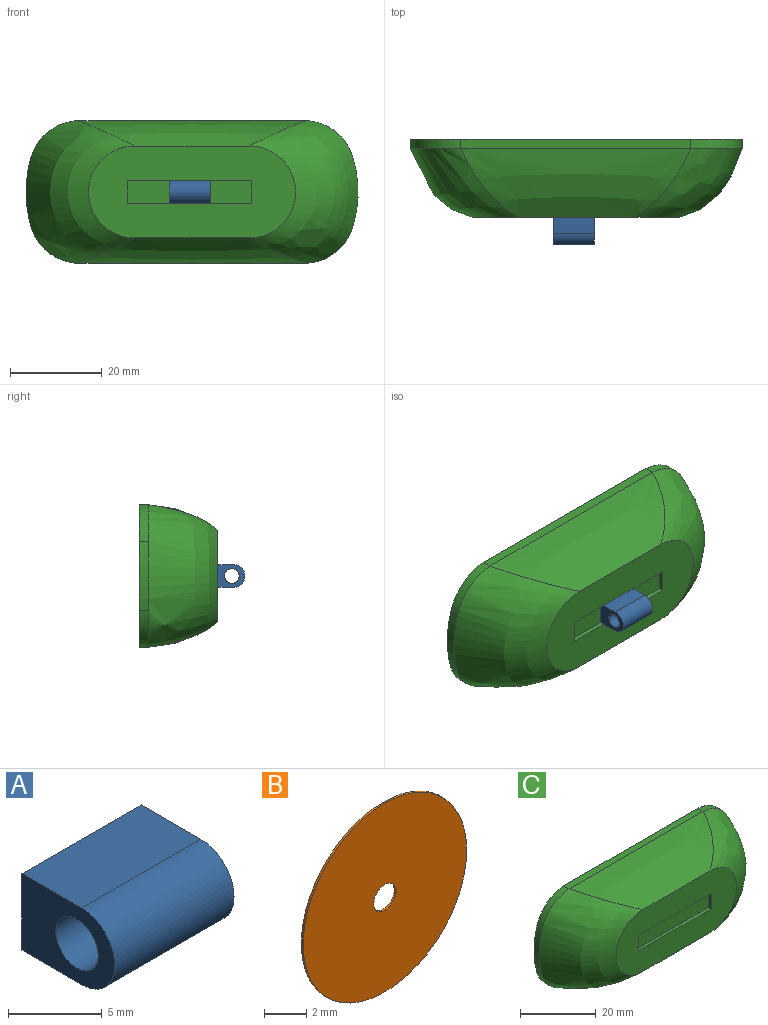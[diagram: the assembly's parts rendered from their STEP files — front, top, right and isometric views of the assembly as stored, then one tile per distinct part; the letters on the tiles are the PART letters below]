
ASSEMBLY  parts=3 mates=2
PART A: 7 faces, bbox 9x7x5 mm
  f0: plane 7x5mm, normal (1,0,0), area 24.3mm2, adj f1,f3,f4,f5,f6
  f1: plane 9x4.5mm, normal (0,0,1), area 40.5mm2, adj f0,f2,f4,f5
  f2: plane 7x5mm, normal (-1,0,0), area 24.3mm2, adj f1,f3,f4,f5,f6
  f3: plane 9x4.5mm, normal (0,0,-1), area 40.5mm2, adj f0,f2,f4,f5
  f4: plane 9x5mm, normal (0,1,0), area 45mm2, adj f0,f1,f2,f3
  f5: cylinder r=2.5mm len=9mm, axis (-1,0,0), area 70.7mm2, adj f0,f1,f2,f3
  f6: cylinder r=1.6mm len=9mm, axis (-1,0,0), area 90.5mm2, adj f0,f2
PART B: 4 faces, bbox 11x0.1x11 mm
  f0: cylinder r=0.75mm len=1.5mm, axis (0,-1,0), area 0.6mm2, adj f2,f3
  f1: cylinder r=5.5mm len=11mm, axis (0,-1,0), area 4.3mm2, adj f2,f3
  f2: plane 11x11mm, normal (0,1,0), area 93.3mm2, adj f0,f1
  f3: plane 11x11mm, normal (0,-1,0), area 93.3mm2, adj f0,f1
PART C: 58 faces, bbox 73.2x17.5x31.6 mm
  f0: plane 45.43x20.43mm, normal (0,-1,0), area 679.2mm2, adj f27,f28,f29,f30,f49,f50,f51,f57
  f1: cylinder r=5.5mm len=11mm, axis (0,-1,0), area 17.3mm2, adj f46,f47
  f2: cylinder r=5.75mm len=11.5mm, axis (0,-1,0), area 18.1mm2, adj f45,f46
  f3: cylinder r=6mm len=12mm, axis (0,1,0), area 37.7mm2, adj f35,f45
  f4: cylinder r=0.5mm len=2mm, axis (0,1,0), area 6.3mm2, adj f35,f36
  f5: cylinder r=0.5mm len=2mm, axis (0,1,0), area 6.3mm2, adj f35,f37
  f6: cylinder r=0.5mm len=2mm, axis (0,1,0), area 6.3mm2, adj f35,f38
  f7: cylinder r=0.5mm len=2mm, axis (0,1,0), area 6.3mm2, adj f35,f39
  f8: cylinder r=0.5mm len=2mm, axis (0,1,0), area 6.3mm2, adj f35,f40
  f9: cylinder r=0.5mm len=2mm, axis (0,1,0), area 6.3mm2, adj f35,f41
  f10: cylinder r=0.5mm len=2mm, axis (0,1,0), area 6.3mm2, adj f35,f42
  f11: cylinder r=0.5mm len=2mm, axis (0,1,0), area 6.3mm2, adj f35,f43
  f12: cylinder r=0.5mm len=2mm, axis (0,1,0), area 6.3mm2, adj f35,f44
  f13: extruded ~15x2mm, area 30.4mm2, adj f14,f20,f21,f30
  f14: cylinder r=11.22mm len=10mm, axis (0,-1,0), area 27.3mm2, adj f13,f15,f21,f30
  f15: plane 50.54x2.54mm, normal (0,0,1), area 100mm2, adj f14,f16,f21,f27
  f16: cylinder r=11.22mm len=10mm, axis (0,-1,0), area 27.3mm2, adj f15,f17,f21,f28
  f17: extruded ~15x2mm, area 30.5mm2, adj f16,f18,f21,f28
  f18: cylinder r=11.22mm len=10mm, axis (0,-1,0), area 27.3mm2, adj f17,f19,f21,f28
  f19: plane 50.54x2.54mm, normal (0,0,-1), area 100mm2, adj f18,f20,f21,f29
  f20: cylinder r=11.22mm len=10mm, axis (0,-1,0), area 27.3mm2, adj f13,f19,f21,f30
  f21: plane 72.64x31mm, normal (0,1,0), area 1626.5mm2, adj f13,f14,f15,f16,f17,f18,f19,f20
  f22: cylinder r=8.17mm len=16mm, axis (0,1,0), area 44.6mm2, adj f21,f23,f25,f26
  f23: plane 20x2mm, normal (0,0,1), area 40mm2, adj f21,f22,f24,f26
  f24: cylinder r=8.17mm len=16mm, axis (0,1,0), area 44.6mm2, adj f21,f23,f25,f26
  f25: plane 20x2mm, normal (0,0,-1), area 40mm2, adj f21,f22,f24,f26
  f26: plane 33.01x16mm, normal (0,1,0), area 9.9mm2, adj f22,f23,f24,f25,f31,f32,f33,f34
  f27: bspline ~50x15mm, area 647.1mm2, adj f0,f15,f28,f30
  f28: bspline ~31.06x23.69mm, area 772mm2, adj f0,f16,f17,f18,f27,f29
  f29: bspline ~50x15mm, area 647.1mm2, adj f0,f19,f28,f30
  f30: bspline ~31.06x23.69mm, area 772.5mm2, adj f0,f13,f14,f20,f27,f29
  f31: cylinder r=8.04mm len=15.8mm, axis (0,-1,0), area 44.5mm2, adj f26,f32,f34,f35
  f32: plane 19.83x2mm, normal (0,0,1), area 39.7mm2, adj f26,f31,f33,f35
  f33: cylinder r=8.05mm len=15.8mm, axis (0,-1,0), area 44.3mm2, adj f26,f32,f34,f35
  f34: plane 19.58x2mm, normal (0,0,-1), area 39.2mm2, adj f26,f31,f33,f35
  f35: plane 32.73x15.8mm, normal (0,1,0), area 339mm2, adj f3,f4,f5,f6,f7,f8,f9,f10
  f36: plane 1x1mm, normal (0,1,0), area 0.8mm2, adj f4
  f37: plane 1x1mm, normal (0,1,0), area 0.8mm2, adj f5
  f38: plane 1x1mm, normal (0,1,0), area 0.8mm2, adj f6
  f39: plane 1x1mm, normal (0,1,0), area 0.8mm2, adj f7
  f40: plane 1x1mm, normal (0,1,0), area 0.8mm2, adj f8
  f41: plane 1x1mm, normal (0,1,0), area 0.8mm2, adj f9
  f42: plane 1x1mm, normal (0,1,0), area 0.8mm2, adj f10
  f43: plane 1x1mm, normal (0,1,0), area 0.8mm2, adj f11
  f44: plane 1x1mm, normal (0,1,0), area 0.8mm2, adj f12
  f45: plane 12x12mm, normal (0,1,0), area 9.2mm2, adj f2,f3
  f46: plane 11.5x11.5mm, normal (0,1,0), area 8.8mm2, adj f1,f2
  f47: plane 11x11mm, normal (0,1,0), area 95mm2, adj f1
  f48: plane 27x5mm, normal (0,-1,0), area 135mm2, adj f49,f50,f51,f57
  f49: plane 27x1mm, normal (0,0,-1), area 27mm2, adj f0,f48,f50,f57
  f50: plane 5x1mm, normal (1,0,0), area 5mm2, adj f0,f48,f49,f51
  f51: plane 27x1mm, normal (0,0,1), area 27mm2, adj f0,f48,f50,f57
  f52: cylinder r=0.31mm len=0.56mm, axis (0,-1,0), area 0mm2, adj f35,f53,f55,f56
  f53: cylinder r=7.27mm len=9.92mm, axis (0,-1,0), area 0.1mm2, adj f35,f52,f54,f56
  f54: cylinder r=0.31mm len=0.56mm, axis (0,-1,0), area 0mm2, adj f35,f53,f55,f56
  f55: cylinder r=6.66mm len=8.91mm, axis (0,-1,0), area 0.1mm2, adj f35,f52,f54,f56
  f56: plane 10.03x2.53mm, normal (0,1,0), area 6.6mm2, adj f52,f53,f54,f55
  f57: plane 5x1mm, normal (-1,0,0), area 5mm2, adj f0,f48,f49,f51
PLACE A t=(0,24.28,0)mm
PLACE B t=(0,22.78,0)mm
PLACE C t=(0,23.28,0)mm
MATE fastened A.f4 <-> C.f48  axis (0,1,0) through (15.55,59.62,59.68)mm
MATE fastened C.f1 <-> B.f0  axis (0,1,0) through (-0.56,73.62,59.68)mm
